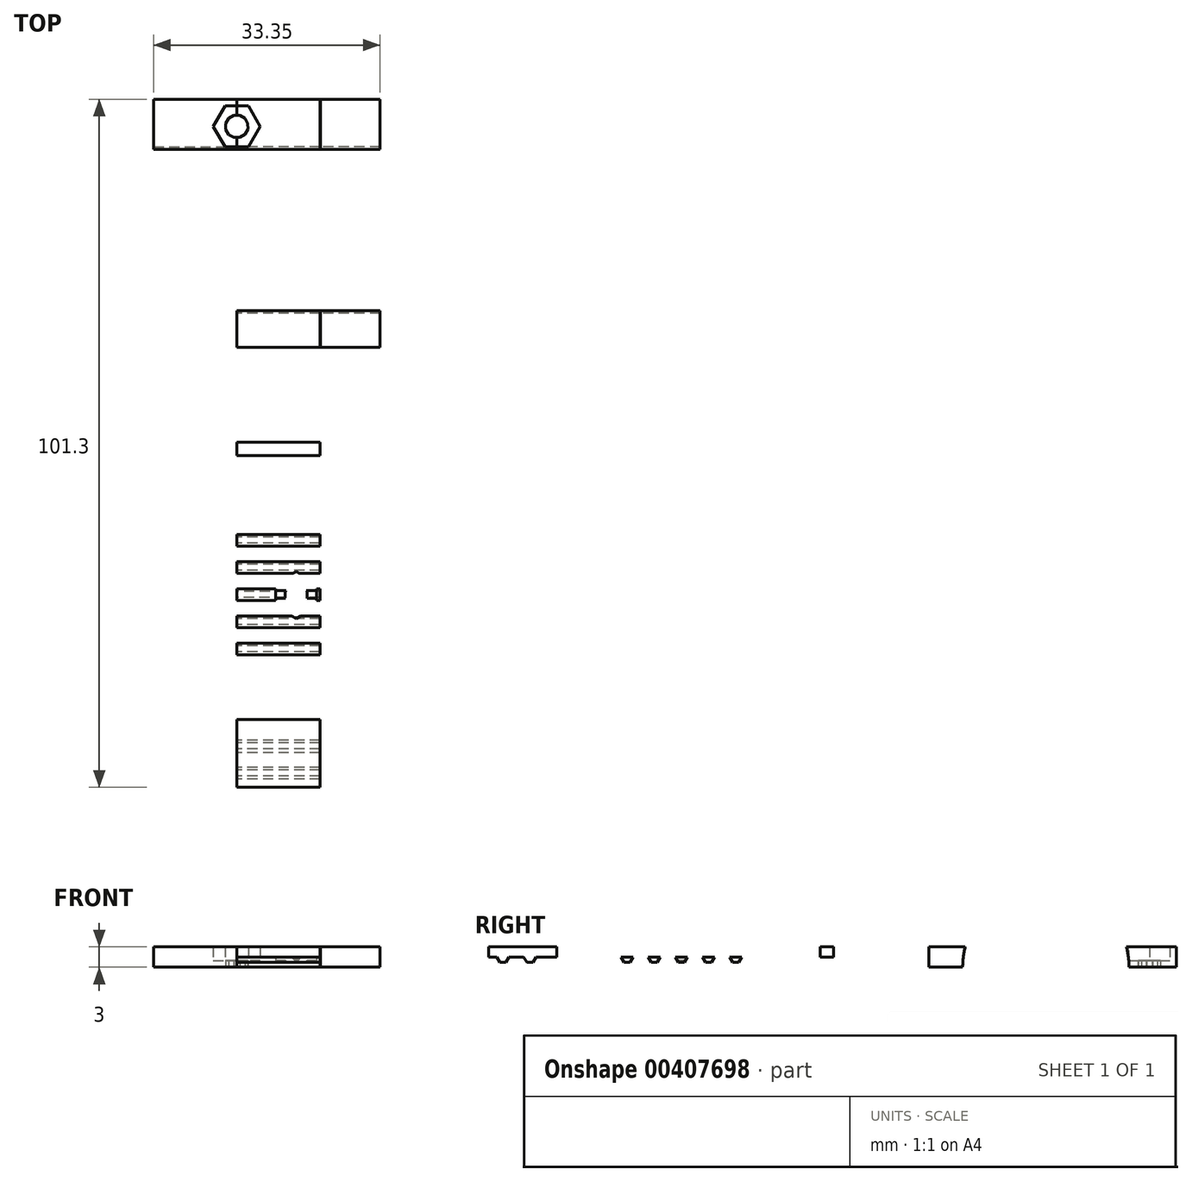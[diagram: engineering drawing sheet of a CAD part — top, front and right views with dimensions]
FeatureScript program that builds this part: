
annotation { "Feature Type Name" : "Feature", "Feature Type Description" : "" }
export const myFeature = defineFeature(function(context is Context, id is Id, definition is map)
    precondition{}
    {
        {
            var Q0;
            Q0=qCreatedBy(makeId("Right.planeOp"),FACE);
            var sketch = newSketch(context, id + "F0", { "sketchPlane" : qUnion([Q0])});
            skLineSegment(sketch, "E0.bottom", {"start": v(-45.88, 3) * mm, "end": v(55.42, 3) * mm});
            skLineSegment(sketch, "E0.top", {"start": v(-45.88, 0) * mm, "end": v(55.42, 0) * mm});
            skLineSegment(sketch, "E0.left", {"start": v(-45.88, 3) * mm, "end": v(-45.88, 0) * mm});
            skLineSegment(sketch, "E0.right", {"start": v(55.42, 3) * mm, "end": v(55.42, 0) * mm});
            skCircle(sketch, "E1", {"center": v(36.17, 0) * mm, "radius": 8.25 * mm});
            skCircle(sketch, "E2", {"center": v(36.17, 0) * mm, "radius": 12.25 * mm});
            skLineSegment(sketch, "E3.bottom", {"start": v(-45.88, 0) * mm, "end": v(18.92, 0) * mm});
            skLineSegment(sketch, "E3.top", {"start": v(-45.88, 1.5) * mm, "end": v(18.92, 1.5) * mm});
            skLineSegment(sketch, "E3.left", {"start": v(-45.88, 0) * mm, "end": v(-45.88, 1.5) * mm});
            skLineSegment(sketch, "E3.right", {"start": v(18.92, 0) * mm, "end": v(18.92, 1.5) * mm});
            skLineSegment(sketch, "E4.bottom", {"start": v(18.92, 1.5) * mm, "end": v(4.92, 1.5) * mm});
            skLineSegment(sketch, "E4.top", {"start": v(18.92, 3) * mm, "end": v(4.92, 3) * mm});
            skLineSegment(sketch, "E4.left", {"start": v(18.92, 1.5) * mm, "end": v(18.92, 3) * mm});
            skLineSegment(sketch, "E4.right", {"start": v(4.92, 1.5) * mm, "end": v(4.92, 3) * mm});
            skLineSegment(sketch, "E5.bottom", {"start": v(-2.58, 1.5) * mm, "end": v(2.92, 1.5) * mm});
            skLineSegment(sketch, "E5.top", {"start": v(-2.58, 3) * mm, "end": v(2.92, 3) * mm});
            skLineSegment(sketch, "E5.left", {"start": v(-2.58, 1.5) * mm, "end": v(-2.58, 3) * mm});
            skLineSegment(sketch, "E5.right", {"start": v(2.92, 1.5) * mm, "end": v(2.92, 3) * mm});
            skLineSegment(sketch, "E6.bottom", {"start": v(-2.58, 1.5) * mm, "end": v(-30.38, 1.5) * mm});
            skLineSegment(sketch, "E6.top", {"start": v(-2.58, 3) * mm, "end": v(-30.38, 3) * mm});
            skLineSegment(sketch, "E6.right", {"start": v(-30.38, 1.5) * mm, "end": v(-30.38, 3) * mm});
            skLineSegment(sketch, "E7.bottom", {"start": v(-30.38, 1.5) * mm, "end": v(-35.88, 1.5) * mm});
            skLineSegment(sketch, "E7.top", {"start": v(-30.38, 3) * mm, "end": v(-35.88, 3) * mm});
            skLineSegment(sketch, "E7.right", {"start": v(-35.88, 1.5) * mm, "end": v(-35.88, 3) * mm});
            skCircle(sketch, "E8.cCircle", {"center": v(-25.51, 1.5) * mm, "radius": 0.87 * mm, "construction": true});
            skLineSegment(sketch, "E8.0", {"start": v(-24.64, 1.5) * mm, "end": v(-25.08, 0.75) * mm});
            skLineSegment(sketch, "E8.1", {"start": v(-25.08, 0.75) * mm, "end": v(-25.94, 0.75) * mm});
            skLineSegment(sketch, "E8.2", {"start": v(-25.94, 0.75) * mm, "end": v(-26.38, 1.5) * mm});
            skLineSegment(sketch, "E9.1.0.0", {"start": v(-21.94, 0.75) * mm, "end": v(-22.38, 1.5) * mm});
            skCircle(sketch, "E9.1.0.3", {"center": v(-21.51, 1.5) * mm, "radius": 0.87 * mm, "construction": true});
            skLineSegment(sketch, "E9.1.0.4", {"start": v(-20.64, 1.5) * mm, "end": v(-21.08, 0.75) * mm});
            skLineSegment(sketch, "E9.1.0.5", {"start": v(-21.08, 0.75) * mm, "end": v(-21.94, 0.75) * mm});
            skLineSegment(sketch, "E9.2.0.0", {"start": v(-17.94, 0.75) * mm, "end": v(-18.38, 1.5) * mm});
            skCircle(sketch, "E9.2.0.3", {"center": v(-17.51, 1.5) * mm, "radius": 0.87 * mm, "construction": true});
            skLineSegment(sketch, "E9.2.0.4", {"start": v(-16.64, 1.5) * mm, "end": v(-17.08, 0.75) * mm});
            skLineSegment(sketch, "E9.2.0.5", {"start": v(-17.08, 0.75) * mm, "end": v(-17.94, 0.75) * mm});
            skLineSegment(sketch, "E9.3.0.0", {"start": v(-13.94, 0.75) * mm, "end": v(-14.38, 1.5) * mm});
            skCircle(sketch, "E9.3.0.3", {"center": v(-13.51, 1.5) * mm, "radius": 0.87 * mm, "construction": true});
            skLineSegment(sketch, "E9.3.0.4", {"start": v(-12.64, 1.5) * mm, "end": v(-13.08, 0.75) * mm});
            skLineSegment(sketch, "E9.3.0.5", {"start": v(-13.08, 0.75) * mm, "end": v(-13.94, 0.75) * mm});
            skLineSegment(sketch, "E9.4.0.0", {"start": v(-9.94, 0.75) * mm, "end": v(-10.38, 1.5) * mm});
            skCircle(sketch, "E9.4.0.3", {"center": v(-9.51, 1.5) * mm, "radius": 0.87 * mm, "construction": true});
            skLineSegment(sketch, "E9.4.0.4", {"start": v(-8.64, 1.5) * mm, "end": v(-9.08, 0.75) * mm});
            skLineSegment(sketch, "E9.4.0.5", {"start": v(-9.08, 0.75) * mm, "end": v(-9.94, 0.75) * mm});
            skLineSegment(sketch, "E9.direction1", {"start": v(-25.94, 0.75) * mm, "end": v(-21.94, 0.75) * mm, "construction": true});
            skCircle(sketch, "E10.cCircle", {"center": v(-43.8, 1.5) * mm, "radius": 0.87 * mm, "construction": true});
            skLineSegment(sketch, "E10.0", {"start": v(-42.93, 1.5) * mm, "end": v(-43.36, 0.75) * mm});
            skLineSegment(sketch, "E10.1", {"start": v(-43.36, 0.75) * mm, "end": v(-44.23, 0.75) * mm});
            skLineSegment(sketch, "E10.2", {"start": v(-44.23, 0.75) * mm, "end": v(-44.66, 1.5) * mm});
            skLineSegment(sketch, "E11.1.0.0", {"start": v(-40.23, 0.75) * mm, "end": v(-40.78, 1.5) * mm});
            skCircle(sketch, "E11.1.0.3", {"center": v(-42.07, 1.5) * mm, "radius": 0.87 * mm, "construction": true});
            skLineSegment(sketch, "E11.1.0.4", {"start": v(-38.93, 1.5) * mm, "end": v(-39.36, 0.75) * mm});
            skLineSegment(sketch, "E11.1.0.5", {"start": v(-39.36, 0.75) * mm, "end": v(-40.23, 0.75) * mm});
            skLineSegment(sketch, "E11.direction1", {"start": v(-44.23, 0.75) * mm, "end": v(-40.23, 0.75) * mm, "construction": true});
            skSolve(sketch);
        }
        {
            var Q0;
            {var subQ0=sQuery(id+"F0.wireOp",EDGE,"E0.right");Q0=makeQuery(id+"F0.imprint","IMPRINT",FACE,{"disambiguationData":[TD([[makeQuery(id+"F0.imprint","IMPRINT",EDGE,{"derivedFrom":subQ0}),-1.0]])]});}
            var Q1;
            {var subQ0=sQuery(id+"F0.wireOp",EDGE,"E2");var subQ1=sQuery(id+"F0.wireOp",EDGE,"E0.bottom");var subQ2=makeQuery(id+"F0.imprint","INTERSECT",VERTEX,{"disambiguationData":[OD(1.0)],"derivedFrom":[subQ1,subQ0]});Q1=makeQuery(id+"F0.imprint","IMPRINT",FACE,{"disambiguationData":[TD([[makeQuery(id+"F0.imprint","IMPRINT",EDGE,{"disambiguationData":[TD([[subQ2,1.0]])],"derivedFrom":subQ1}),-1.0]])]});}
            var Q2;
            {var subQ0=sQuery(id+"F0.wireOp",EDGE,"E2");var subQ1=sQuery(id+"F0.wireOp",EDGE,"E0.bottom");var subQ2=makeQuery(id+"F0.imprint","INTERSECT",VERTEX,{"disambiguationData":[OD(0.0)],"derivedFrom":[subQ1,subQ0]});Q2=makeQuery(id+"F0.imprint","IMPRINT",FACE,{"disambiguationData":[TD([[makeQuery(id+"F0.imprint","IMPRINT",EDGE,{"disambiguationData":[TD([[subQ2,-1.0]])],"derivedFrom":subQ1}),1.0]])]});}
            var Q3;
            {var subQ0=sQuery(id+"F0.wireOp",EDGE,"E2");var subQ1=sQuery(id+"F0.wireOp",EDGE,"E0.bottom");var subQ2=makeQuery(id+"F0.imprint","INTERSECT",VERTEX,{"disambiguationData":[OD(0.0)],"derivedFrom":[subQ1,subQ0]});Q3=makeQuery(id+"F0.imprint","IMPRINT",FACE,{"disambiguationData":[TD([[makeQuery(id+"F0.imprint","IMPRINT",EDGE,{"disambiguationData":[TD([[subQ2,-1.0]])],"derivedFrom":subQ1}),-1.0]])]});}
            var Q4;
            {var subQ0=sQuery(id+"F0.wireOp",EDGE,"E3.right");Q4=makeQuery(id+"F0.imprint","IMPRINT",FACE,{"disambiguationData":[TD([[makeQuery(id+"F0.imprint","IMPRINT",EDGE,{"derivedFrom":subQ0}),-1.0]])]});}
            var Q5;
            Q5=makeQuery(id+"F0.imprint","IMPRINT",FACE,{"disambiguationData":[TD([[makeQuery(id+"F0.imprint","IMPRINT",EDGE,{"derivedFrom":sQuery(id+"F0.wireOp",EDGE,"E4.bottom")}),-1.0]])]});
            var Q6;
            {var subQ0=sQuery(id+"F0.wireOp",EDGE,"E4.right");Q6=makeQuery(id+"F0.imprint","IMPRINT",FACE,{"disambiguationData":[TD([[makeQuery(id+"F0.imprint","IMPRINT",EDGE,{"derivedFrom":subQ0}),1.0]])]});}
            var Q7;
            Q7=makeQuery(id+"F0.imprint","IMPRINT",FACE,{"disambiguationData":[TD([[makeQuery(id+"F0.imprint","IMPRINT",EDGE,{"derivedFrom":sQuery(id+"F0.wireOp",EDGE,"E3.bottom")}),1.0]])]});
            var Q8;
            Q8=makeQuery(id+"F0.imprint","IMPRINT",FACE,{"disambiguationData":[TD([[makeQuery(id+"F0.imprint","IMPRINT",EDGE,{"derivedFrom":sQuery(id+"F0.wireOp",EDGE,"E5.bottom")}),1.0]])]});
            var Q9;
            Q9=makeQuery(id+"F0.imprint","IMPRINT",FACE,{"disambiguationData":[TD([[makeQuery(id+"F0.imprint","IMPRINT",EDGE,{"derivedFrom":sQuery(id+"F0.wireOp",EDGE,"E6.top")}),1.0]])]});
            var Q10;
            {var subQ0=sQuery(id+"F0.wireOp",EDGE,"E9.4.0.0");Q10=makeQuery(id+"F0.imprint","IMPRINT",FACE,{"disambiguationData":[TD([[makeQuery(id+"F0.imprint","IMPRINT",EDGE,{"derivedFrom":subQ0}),-1.0]])]});}
            var Q11;
            {var subQ0=sQuery(id+"F0.wireOp",EDGE,"E9.3.0.0");Q11=makeQuery(id+"F0.imprint","IMPRINT",FACE,{"disambiguationData":[TD([[makeQuery(id+"F0.imprint","IMPRINT",EDGE,{"derivedFrom":subQ0}),-1.0]])]});}
            var Q12;
            {var subQ0=sQuery(id+"F0.wireOp",EDGE,"E9.2.0.0");Q12=makeQuery(id+"F0.imprint","IMPRINT",FACE,{"disambiguationData":[TD([[makeQuery(id+"F0.imprint","IMPRINT",EDGE,{"derivedFrom":subQ0}),-1.0]])]});}
            var Q13;
            {var subQ0=sQuery(id+"F0.wireOp",EDGE,"E9.1.0.0");Q13=makeQuery(id+"F0.imprint","IMPRINT",FACE,{"disambiguationData":[TD([[makeQuery(id+"F0.imprint","IMPRINT",EDGE,{"derivedFrom":subQ0}),-1.0]])]});}
            var Q14;
            {var subQ0=sQuery(id+"F0.wireOp",EDGE,"E11.1.0.0");Q14=makeQuery(id+"F0.imprint","IMPRINT",FACE,{"disambiguationData":[TD([[makeQuery(id+"F0.imprint","IMPRINT",EDGE,{"derivedFrom":subQ0}),-1.0]])]});}
            var Q15;
            {var subQ3=sQuery(id+"F0.wireOp",EDGE,"E0.left");Q15=makeQuery(id+"F0.imprint","IMPRINT",FACE,{"disambiguationData":[TD([[makeQuery(id+"F0.imprint","IMPRINT",EDGE,{"derivedFrom":subQ3}),1.0]])]});}
            var Q16;
            Q16=makeQuery(id+"F0.imprint","IMPRINT",FACE,{"disambiguationData":[TD([[makeQuery(id+"F0.imprint","IMPRINT",EDGE,{"derivedFrom":sQuery(id+"F0.wireOp",EDGE,"E7.bottom")}),-1.0]])]});
            var Q17;
            {var subQ0=sQuery(id+"F0.wireOp",EDGE,"E10.0");Q17=makeQuery(id+"F0.imprint","IMPRINT",FACE,{"disambiguationData":[TD([[makeQuery(id+"F0.imprint","IMPRINT",EDGE,{"derivedFrom":subQ0}),-1.0]])]});}
            var Q18;
            {var subQ0=sQuery(id+"F0.wireOp",EDGE,"E8.0");Q18=makeQuery(id+"F0.imprint","IMPRINT",FACE,{"disambiguationData":[TD([[makeQuery(id+"F0.imprint","IMPRINT",EDGE,{"derivedFrom":subQ0}),-1.0]])]});}
            extrude(context, id + "F1", {"entities" : qUnion([Q0, Q1, Q2, Q3, Q4, Q5, Q6, Q7, Q8, Q9, Q10, Q11, Q12, Q13, Q14, Q15, Q16, Q17, Q18]), "depth" : 12.25 * mm, "hasSecondDirection" : true, "secondDirectionOppositeDirection" : false, "secondDirectionDepth" : 6.75 * mm});
        }
        {
            var Q0;
            {var subQ0=sQuery(id+"F0.wireOp",EDGE,"E3.right");Q0=makeQuery(id+"F0.imprint","IMPRINT",FACE,{"disambiguationData":[TD([[makeQuery(id+"F0.imprint","IMPRINT",EDGE,{"derivedFrom":subQ0}),-1.0]])]});}
            var Q1;
            {var subQ0=sQuery(id+"F0.wireOp",EDGE,"E2");var subQ1=sQuery(id+"F0.wireOp",EDGE,"E0.bottom");var subQ2=makeQuery(id+"F0.imprint","INTERSECT",VERTEX,{"disambiguationData":[OD(0.0)],"derivedFrom":[subQ1,subQ0]});Q1=makeQuery(id+"F0.imprint","IMPRINT",FACE,{"disambiguationData":[TD([[makeQuery(id+"F0.imprint","IMPRINT",EDGE,{"disambiguationData":[TD([[subQ2,-1.0]])],"derivedFrom":subQ1}),-1.0]])]});}
            var Q2;
            {var subQ0=sQuery(id+"F0.wireOp",EDGE,"E2");var subQ1=sQuery(id+"F0.wireOp",EDGE,"E0.bottom");var subQ2=makeQuery(id+"F0.imprint","INTERSECT",VERTEX,{"disambiguationData":[OD(0.0)],"derivedFrom":[subQ1,subQ0]});Q2=makeQuery(id+"F0.imprint","IMPRINT",FACE,{"disambiguationData":[TD([[makeQuery(id+"F0.imprint","IMPRINT",EDGE,{"disambiguationData":[TD([[subQ2,-1.0]])],"derivedFrom":subQ1}),1.0]])]});}
            var Q3;
            {var subQ0=sQuery(id+"F0.wireOp",EDGE,"E2");var subQ1=sQuery(id+"F0.wireOp",EDGE,"E0.bottom");var subQ2=makeQuery(id+"F0.imprint","INTERSECT",VERTEX,{"disambiguationData":[OD(1.0)],"derivedFrom":[subQ1,subQ0]});Q3=makeQuery(id+"F0.imprint","IMPRINT",FACE,{"disambiguationData":[TD([[makeQuery(id+"F0.imprint","IMPRINT",EDGE,{"disambiguationData":[TD([[subQ2,1.0]])],"derivedFrom":subQ1}),-1.0]])]});}
            var Q4;
            {var subQ0=sQuery(id+"F0.wireOp",EDGE,"E0.right");Q4=makeQuery(id+"F0.imprint","IMPRINT",FACE,{"disambiguationData":[TD([[makeQuery(id+"F0.imprint","IMPRINT",EDGE,{"derivedFrom":subQ0}),-1.0]])]});}
            var Q5;
            {var subQ0=sQuery(id+"F0.wireOp",EDGE,"E4.right");Q5=makeQuery(id+"F0.imprint","IMPRINT",FACE,{"disambiguationData":[TD([[makeQuery(id+"F0.imprint","IMPRINT",EDGE,{"derivedFrom":subQ0}),1.0]])]});}
            var Q6;
            Q6=makeQuery(id+"F0.imprint","IMPRINT",FACE,{"disambiguationData":[TD([[makeQuery(id+"F0.imprint","IMPRINT",EDGE,{"derivedFrom":sQuery(id+"F0.wireOp",EDGE,"E6.top")}),1.0]])]});
            var Q7;
            {var subQ0=sQuery(id+"F0.wireOp",EDGE,"E9.4.0.0");Q7=makeQuery(id+"F0.imprint","IMPRINT",FACE,{"disambiguationData":[TD([[makeQuery(id+"F0.imprint","IMPRINT",EDGE,{"derivedFrom":subQ0}),-1.0]])]});}
            var Q8;
            {var subQ0=sQuery(id+"F0.wireOp",EDGE,"E9.3.0.0");Q8=makeQuery(id+"F0.imprint","IMPRINT",FACE,{"disambiguationData":[TD([[makeQuery(id+"F0.imprint","IMPRINT",EDGE,{"derivedFrom":subQ0}),-1.0]])]});}
            var Q9;
            {var subQ0=sQuery(id+"F0.wireOp",EDGE,"E9.2.0.0");Q9=makeQuery(id+"F0.imprint","IMPRINT",FACE,{"disambiguationData":[TD([[makeQuery(id+"F0.imprint","IMPRINT",EDGE,{"derivedFrom":subQ0}),-1.0]])]});}
            var Q10;
            {var subQ0=sQuery(id+"F0.wireOp",EDGE,"E9.1.0.0");Q10=makeQuery(id+"F0.imprint","IMPRINT",FACE,{"disambiguationData":[TD([[makeQuery(id+"F0.imprint","IMPRINT",EDGE,{"derivedFrom":subQ0}),-1.0]])]});}
            var Q11;
            {var subQ0=sQuery(id+"F0.wireOp",EDGE,"E8.0");Q11=makeQuery(id+"F0.imprint","IMPRINT",FACE,{"disambiguationData":[TD([[makeQuery(id+"F0.imprint","IMPRINT",EDGE,{"derivedFrom":subQ0}),-1.0]])]});}
            var Q12;
            {var subQ3=sQuery(id+"F0.wireOp",EDGE,"E0.left");Q12=makeQuery(id+"F0.imprint","IMPRINT",FACE,{"disambiguationData":[TD([[makeQuery(id+"F0.imprint","IMPRINT",EDGE,{"derivedFrom":subQ3}),1.0]])]});}
            var Q13;
            {var subQ0=sQuery(id+"F0.wireOp",EDGE,"E10.0");Q13=makeQuery(id+"F0.imprint","IMPRINT",FACE,{"disambiguationData":[TD([[makeQuery(id+"F0.imprint","IMPRINT",EDGE,{"derivedFrom":subQ0}),-1.0]])]});}
            var Q14;
            {var subQ0=sQuery(id+"F0.wireOp",EDGE,"E11.1.0.0");Q14=makeQuery(id+"F0.imprint","IMPRINT",FACE,{"disambiguationData":[TD([[makeQuery(id+"F0.imprint","IMPRINT",EDGE,{"derivedFrom":subQ0}),-1.0]])]});}
            extrude(context, id + "F2", {"entities" : qUnion([Q0, Q1, Q2, Q3, Q4, Q5, Q6, Q7, Q8, Q9, Q10, Q11, Q12, Q13, Q14]), "operationType" : NewBodyOperationType.ADD, "depth" : 6.75 * mm});
        }
        {
            var Q0;
            Q0=makeQuery(id+"F1.opExtrude","SWEPT_BODY",BODY,{"disambiguationData":[OSD([sQuery(id+"F0.wireOp",EDGE,"E0.bottom"),sQuery(id+"F0.wireOp",EDGE,"E0.top"),sQuery(id+"F0.wireOp",EDGE,"E0.left"),sQuery(id+"F0.wireOp",EDGE,"E0.right"),sQuery(id+"F0.wireOp",EDGE,"E1"),sQuery(id+"F0.wireOp",EDGE,"E2"),sQuery(id+"F0.wireOp",EDGE,"E3.bottom"),sQuery(id+"F0.wireOp",EDGE,"E3.left"),sQuery(id+"F0.wireOp",EDGE,"E4.top"),sQuery(id+"F0.wireOp",EDGE,"E5.top"),sQuery(id+"F0.wireOp",EDGE,"E6.top"),sQuery(id+"F0.wireOp",EDGE,"E7.top")])]});
            var Q1;
            Q1=qCreatedBy(makeId("Right.planeOp"),FACE);
            mirror(context, id + "F3", {"operationType" : NewBodyOperationType.ADD, "entities" : qUnion([Q0]), "mirrorPlane" : qUnion([Q1])});
        }
        {
            var Q0;
            Q0=qCreatedBy(makeId("Top.planeOp"),FACE);
            var sketch = newSketch(context, id + "F4", { "sketchPlane" : qUnion([Q0])});
            skCircle(sketch, "E12.cCircle", {"center": v(0, 51.42) * mm, "radius": 3 * mm, "construction": true});
            skLineSegment(sketch, "E12.0", {"start": v(3.46, 51.42) * mm, "end": v(1.73, 48.42) * mm});
            skLineSegment(sketch, "E12.1", {"start": v(1.73, 48.42) * mm, "end": v(-1.73, 48.42) * mm});
            skLineSegment(sketch, "E12.2", {"start": v(-1.73, 48.42) * mm, "end": v(-3.46, 51.42) * mm});
            skLineSegment(sketch, "E12.3", {"start": v(-3.46, 51.42) * mm, "end": v(-1.73, 54.42) * mm});
            skLineSegment(sketch, "E12.4", {"start": v(-1.73, 54.42) * mm, "end": v(1.73, 54.42) * mm});
            skLineSegment(sketch, "E12.5", {"start": v(1.73, 54.42) * mm, "end": v(3.46, 51.42) * mm});
            skPoint(sketch, "E12.0.midPoint", {"position": v(2.6, 49.92) * mm});
            skCircle(sketch, "E13.cCircle", {"center": v(0, 51.42) * mm, "radius": 1.63 * mm, "construction": true});
            skLineSegment(sketch, "E13.0", {"start": v(1.18, 52.62) * mm, "end": v(1.62, 51.87) * mm});
            skLineSegment(sketch, "E13.1", {"start": v(1.62, 51.87) * mm, "end": v(1.63, 51) * mm});
            skLineSegment(sketch, "E13.2", {"start": v(1.63, 51) * mm, "end": v(1.2, 50.24) * mm});
            skLineSegment(sketch, "E13.3", {"start": v(1.2, 50.24) * mm, "end": v(0.45, 49.8) * mm});
            skLineSegment(sketch, "E13.4", {"start": v(0.45, 49.8) * mm, "end": v(-0.42, 49.8) * mm});
            skLineSegment(sketch, "E13.5", {"start": v(-0.42, 49.8) * mm, "end": v(-1.18, 50.22) * mm});
            skLineSegment(sketch, "E13.6", {"start": v(-1.18, 50.22) * mm, "end": v(-1.62, 50.97) * mm});
            skLineSegment(sketch, "E13.7", {"start": v(-1.62, 50.97) * mm, "end": v(-1.63, 51.84) * mm});
            skLineSegment(sketch, "E13.8", {"start": v(-1.63, 51.84) * mm, "end": v(-1.2, 52.6) * mm});
            skLineSegment(sketch, "E13.9", {"start": v(-1.2, 52.6) * mm, "end": v(-0.45, 53.04) * mm});
            skLineSegment(sketch, "E13.10", {"start": v(-0.45, 53.04) * mm, "end": v(0.42, 53.05) * mm});
            skLineSegment(sketch, "E13.11", {"start": v(0.42, 53.05) * mm, "end": v(1.18, 52.62) * mm});
            skPoint(sketch, "E13.0.midPoint", {"position": v(1.4, 52.25) * mm});
            skCircle(sketch, "E14.cCircle", {"center": v(8.75, -17.58) * mm, "radius": 3 * mm, "construction": true});
            skLineSegment(sketch, "E14.0", {"start": v(8.75, -14.11) * mm, "end": v(11.75, -15.84) * mm});
            skLineSegment(sketch, "E14.1", {"start": v(11.75, -15.84) * mm, "end": v(11.75, -19.3) * mm});
            skLineSegment(sketch, "E14.2", {"start": v(11.75, -19.3) * mm, "end": v(8.75, -21.04) * mm});
            skLineSegment(sketch, "E14.3", {"start": v(8.75, -21.04) * mm, "end": v(5.75, -19.3) * mm});
            skLineSegment(sketch, "E14.4", {"start": v(5.75, -19.3) * mm, "end": v(5.75, -15.84) * mm});
            skLineSegment(sketch, "E14.5", {"start": v(5.75, -15.84) * mm, "end": v(8.75, -14.11) * mm});
            skPoint(sketch, "E14.0.midPoint", {"position": v(10.25, -14.98) * mm});
            skCircle(sketch, "E15.cCircle", {"center": v(8.75, -17.58) * mm, "radius": 1.63 * mm, "construction": true});
            skLineSegment(sketch, "E15.0", {"start": v(7.55, -16.4) * mm, "end": v(8.3, -15.96) * mm});
            skLineSegment(sketch, "E15.1", {"start": v(8.3, -15.96) * mm, "end": v(9.17, -15.95) * mm});
            skLineSegment(sketch, "E15.2", {"start": v(9.17, -15.95) * mm, "end": v(9.93, -16.38) * mm});
            skLineSegment(sketch, "E15.3", {"start": v(9.93, -16.38) * mm, "end": v(10.37, -17.13) * mm});
            skLineSegment(sketch, "E15.4", {"start": v(10.37, -17.13) * mm, "end": v(10.38, -18) * mm});
            skLineSegment(sketch, "E15.5", {"start": v(10.38, -18) * mm, "end": v(9.95, -18.76) * mm});
            skLineSegment(sketch, "E15.6", {"start": v(9.95, -18.76) * mm, "end": v(9.2, -19.2) * mm});
            skLineSegment(sketch, "E15.7", {"start": v(9.2, -19.2) * mm, "end": v(8.33, -19.2) * mm});
            skLineSegment(sketch, "E15.8", {"start": v(8.33, -19.2) * mm, "end": v(7.57, -18.78) * mm});
            skLineSegment(sketch, "E15.9", {"start": v(7.57, -18.78) * mm, "end": v(7.13, -18.03) * mm});
            skLineSegment(sketch, "E15.10", {"start": v(7.13, -18.03) * mm, "end": v(7.12, -17.16) * mm});
            skLineSegment(sketch, "E15.11", {"start": v(7.12, -17.16) * mm, "end": v(7.55, -16.4) * mm});
            skPoint(sketch, "E15.0.midPoint", {"position": v(7.93, -16.18) * mm});
            skLineSegment(sketch, "E16.MirrorCS", {"start": v(-7.13, -18.03) * mm, "end": v(-7.12, -17.16) * mm});
            skLineSegment(sketch, "E17.MirrorCS", {"start": v(-8.3, -15.96) * mm, "end": v(-9.17, -15.95) * mm});
            skLineSegment(sketch, "E18.MirrorCS", {"start": v(-10.37, -17.13) * mm, "end": v(-10.38, -18) * mm});
            skLineSegment(sketch, "E19.MirrorCS", {"start": v(-7.12, -17.16) * mm, "end": v(-7.55, -16.4) * mm});
            skLineSegment(sketch, "E20.MirrorCS", {"start": v(-10.38, -18) * mm, "end": v(-9.95, -18.76) * mm});
            skLineSegment(sketch, "E21.MirrorCS", {"start": v(-9.93, -16.38) * mm, "end": v(-10.37, -17.13) * mm});
            skLineSegment(sketch, "E22.MirrorCS", {"start": v(-9.17, -15.95) * mm, "end": v(-9.93, -16.38) * mm});
            skLineSegment(sketch, "E23.MirrorCS", {"start": v(-7.57, -18.78) * mm, "end": v(-7.13, -18.03) * mm});
            skLineSegment(sketch, "E24.MirrorCS", {"start": v(-9.95, -18.76) * mm, "end": v(-9.2, -19.2) * mm});
            skLineSegment(sketch, "E25.MirrorCS", {"start": v(-8.33, -19.2) * mm, "end": v(-7.57, -18.78) * mm});
            skCircle(sketch, "E26.MirrorC", {"center": v(-8.75, -17.58) * mm, "radius": 1.63 * mm, "construction": true});
            skLineSegment(sketch, "E27.MirrorCS", {"start": v(-9.2, -19.2) * mm, "end": v(-8.33, -19.2) * mm});
            skLineSegment(sketch, "E28.MirrorCS", {"start": v(-7.55, -16.4) * mm, "end": v(-8.3, -15.96) * mm});
            skLineSegment(sketch, "E29.MirrorCS", {"start": v(-8.75, -14.11) * mm, "end": v(-11.75, -15.84) * mm});
            skLineSegment(sketch, "E30.MirrorCS", {"start": v(-11.75, -15.84) * mm, "end": v(-11.75, -19.3) * mm});
            skLineSegment(sketch, "E31.MirrorCS", {"start": v(-5.75, -19.3) * mm, "end": v(-5.75, -15.84) * mm});
            skPoint(sketch, "E32.MirrorP", {"position": v(-7.93, -16.18) * mm});
            skCircle(sketch, "E33.MirrorC", {"center": v(-8.75, -17.58) * mm, "radius": 3 * mm, "construction": true});
            skLineSegment(sketch, "E34.MirrorCS", {"start": v(-8.75, -21.04) * mm, "end": v(-5.75, -19.3) * mm});
            skLineSegment(sketch, "E35.MirrorCS", {"start": v(-5.75, -15.84) * mm, "end": v(-8.75, -14.11) * mm});
            skLineSegment(sketch, "E36.MirrorCS", {"start": v(-11.75, -19.3) * mm, "end": v(-8.75, -21.04) * mm});
            skPoint(sketch, "E37.MirrorP", {"position": v(-10.25, -14.98) * mm});
            skSolve(sketch);
        }
        {
            var Q0;
            Q0=makeQuery(id+"F4.imprint","IMPRINT",FACE,{"disambiguationData":[TD([[makeQuery(id+"F4.imprint","IMPRINT",EDGE,{"derivedFrom":sQuery(id+"F4.wireOp",EDGE,"E16.MirrorCS")}),1.0]])]});
            var Q1;
            Q1=makeQuery(id+"F4.imprint","IMPRINT",FACE,{"disambiguationData":[TD([[makeQuery(id+"F4.imprint","IMPRINT",EDGE,{"derivedFrom":sQuery(id+"F4.wireOp",EDGE,"E15.0")}),-1.0]])]});
            var Q2;
            Q2=makeQuery(id+"F4.imprint","IMPRINT",FACE,{"disambiguationData":[TD([[makeQuery(id+"F4.imprint","IMPRINT",EDGE,{"derivedFrom":sQuery(id+"F4.wireOp",EDGE,"E13.0")}),-1.0]])]});
            extrude(context, id + "F5", {"entities" : qUnion([Q0, Q1, Q2]), "operationType" : NewBodyOperationType.REMOVE, "depth" : 6 * mm});
        }
        {
            var Q0;
            Q0=makeQuery(id+"F4.imprint","IMPRINT",FACE,{"disambiguationData":[TD([[makeQuery(id+"F4.imprint","IMPRINT",EDGE,{"derivedFrom":sQuery(id+"F4.wireOp",EDGE,"E12.0")}),-1.0]])]});
            var Q1;
            Q1=makeQuery(id+"F4.imprint","IMPRINT",FACE,{"disambiguationData":[TD([[makeQuery(id+"F4.imprint","IMPRINT",EDGE,{"derivedFrom":sQuery(id+"F4.wireOp",EDGE,"E16.MirrorCS")}),-1.0]])]});
            var Q2;
            Q2=makeQuery(id+"F4.imprint","IMPRINT",FACE,{"disambiguationData":[TD([[makeQuery(id+"F4.imprint","IMPRINT",EDGE,{"derivedFrom":sQuery(id+"F4.wireOp",EDGE,"E14.0")}),-1.0]])]});
            extrude(context, id + "F6", {"entities" : qUnion([Q0, Q1, Q2]), "operationType" : NewBodyOperationType.REMOVE, "depth" : 25 * mm, "hasSecondDirection" : true, "secondDirectionOppositeDirection" : false, "secondDirectionDepth" : 1 * mm});
        }
        {
            var Q0;
            {var subQ0=sQuery(id+"F0.wireOp",EDGE,"E2");var subQ1=sQuery(id+"F0.wireOp",EDGE,"E0.bottom");var subQ2=makeQuery(id+"F0.imprint","INTERSECT",VERTEX,{"disambiguationData":[OD(0.0)],"derivedFrom":[subQ1,subQ0]});Q0=makeQuery(id+"F0.imprint","IMPRINT",FACE,{"disambiguationData":[TD([[makeQuery(id+"F0.imprint","IMPRINT",EDGE,{"disambiguationData":[TD([[subQ2,-1.0]])],"derivedFrom":subQ1}),1.0]])]});}
            var Q1;
            {var subQ0=sQuery(id+"F0.wireOp",EDGE,"E2");var subQ1=sQuery(id+"F0.wireOp",EDGE,"E0.bottom");var subQ2=makeQuery(id+"F0.imprint","INTERSECT",VERTEX,{"disambiguationData":[OD(0.0)],"derivedFrom":[subQ1,subQ0]});Q1=makeQuery(id+"F0.imprint","IMPRINT",FACE,{"disambiguationData":[TD([[makeQuery(id+"F0.imprint","IMPRINT",EDGE,{"disambiguationData":[TD([[subQ2,-1.0]])],"derivedFrom":subQ1}),-1.0]])]});}
            var Q2;
            {var subQ0=sQuery(id+"F0.wireOp",EDGE,"E2");var subQ1=sQuery(id+"F0.wireOp",EDGE,"E0.bottom");var subQ2=makeQuery(id+"F0.imprint","INTERSECT",VERTEX,{"disambiguationData":[OD(1.0)],"derivedFrom":[subQ1,subQ0]});Q2=makeQuery(id+"F0.imprint","IMPRINT",FACE,{"disambiguationData":[TD([[makeQuery(id+"F0.imprint","IMPRINT",EDGE,{"disambiguationData":[TD([[subQ2,1.0]])],"derivedFrom":subQ1}),-1.0]])]});}
            var Q3;
            {var subQ0=sQuery(id+"F0.wireOp",EDGE,"E2");var subQ1=sQuery(id+"F0.wireOp",EDGE,"E0.top");var subQ2=makeQuery(id+"F0.imprint","INTERSECT",VERTEX,{"disambiguationData":[OD(0.0)],"derivedFrom":[subQ1,subQ0]});Q3=makeQuery(id+"F0.imprint","IMPRINT",FACE,{"disambiguationData":[TD([[makeQuery(id+"F0.imprint","IMPRINT",EDGE,{"disambiguationData":[TD([[subQ2,-1.0]])],"derivedFrom":subQ1}),-1.0]])]});}
            extrude(context, id + "F7", {"entities" : qUnion([Q0, Q1, Q2, Q3]), "depth" : 21.1 * mm, "hasSecondDirection" : true, "secondDirectionOppositeDirection" : false, "secondDirectionDepth" : 12.3 * mm});
        }
    });
